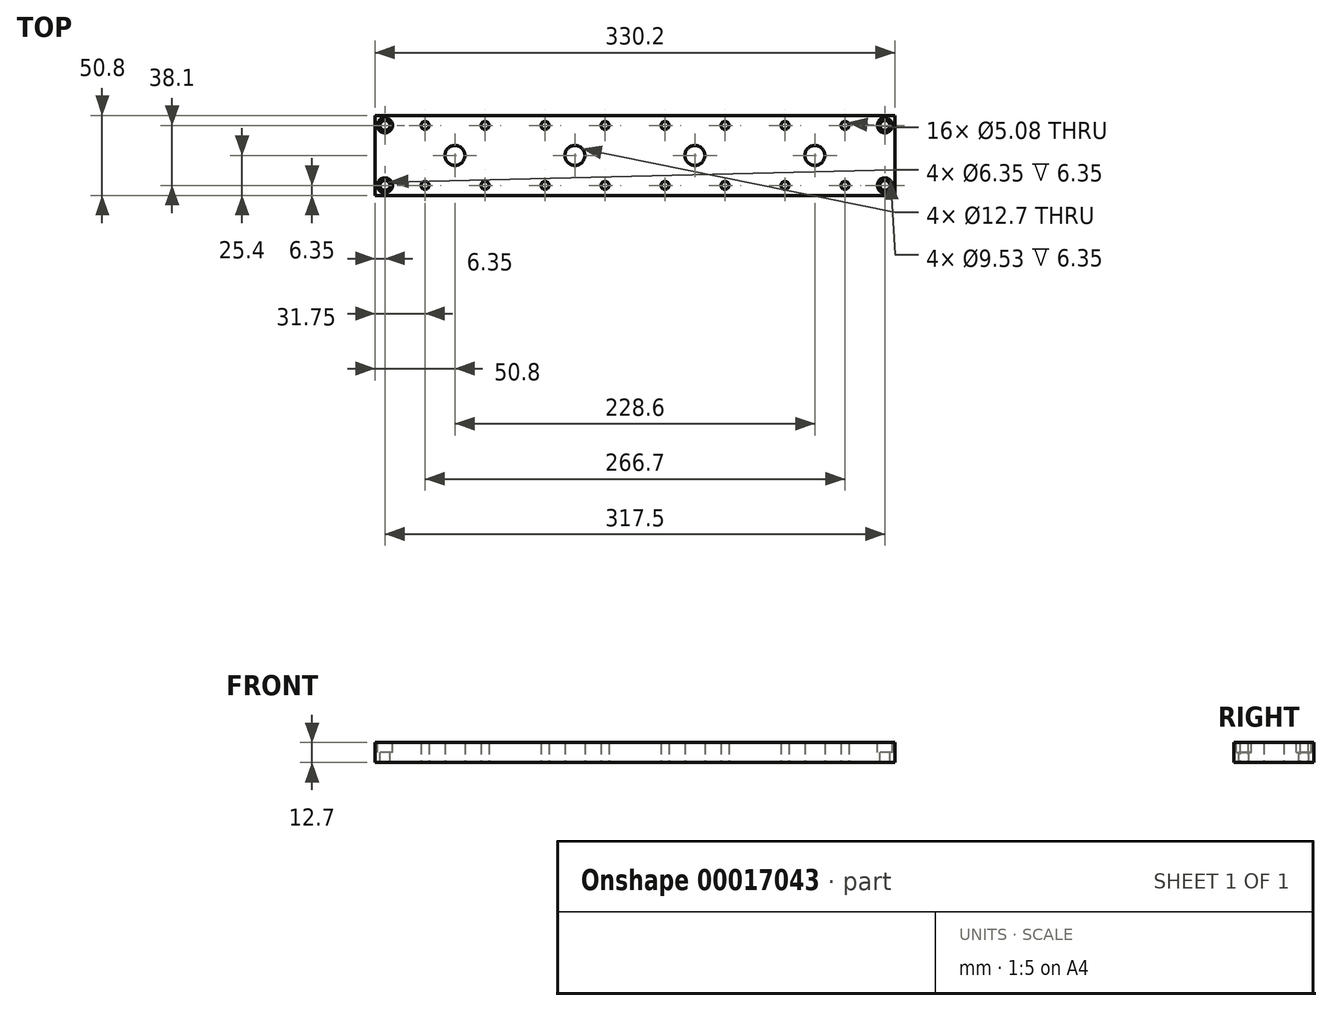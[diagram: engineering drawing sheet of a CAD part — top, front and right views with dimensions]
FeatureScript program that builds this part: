
annotation { "Feature Type Name" : "Feature", "Feature Type Description" : "" }
export const myFeature = defineFeature(function(context is Context, id is Id, definition is map)
    precondition{}
    {
        {
            var Q0;
            Q0=qCreatedBy(makeId("Top.planeOp"),FACE);
            var sketch = newSketch(context, id + "F0", { "sketchPlane" : qUnion([Q0])});
            skLineSegment(sketch, "E0.bottom", {"start": v(165.1, 25.4) * mm, "end": v(-165.1, 25.4) * mm});
            skLineSegment(sketch, "E0.top", {"start": v(165.1, -25.4) * mm, "end": v(-165.1, -25.4) * mm});
            skLineSegment(sketch, "E0.left", {"start": v(165.1, 25.4) * mm, "end": v(165.1, -25.4) * mm});
            skLineSegment(sketch, "E0.right", {"start": v(-165.1, 25.4) * mm, "end": v(-165.1, -25.4) * mm});
            skPoint(sketch, "E0.middle", {"position": v(0, 0) * mm});
            skCircle(sketch, "E1", {"center": v(-38.1, 0) * mm, "radius": 6.35 * mm});
            skCircle(sketch, "E2", {"center": v(-114.3, 0) * mm, "radius": 6.35 * mm});
            skCircle(sketch, "E3", {"center": v(38.1, 0) * mm, "radius": 6.35 * mm});
            skCircle(sketch, "E4", {"center": v(114.3, 0) * mm, "radius": 6.35 * mm});
            skCircle(sketch, "E5", {"center": v(-133.35, 19.05) * mm, "radius": 2.54 * mm});
            skCircle(sketch, "E6", {"center": v(-95.25, 19.05) * mm, "radius": 2.54 * mm});
            skCircle(sketch, "E7", {"center": v(-95.25, -19.05) * mm, "radius": 2.54 * mm});
            skCircle(sketch, "E8", {"center": v(-133.35, -19.05) * mm, "radius": 2.54 * mm});
            skCircle(sketch, "E9.1.0.0", {"center": v(-19.05, 19.05) * mm, "radius": 2.54 * mm});
            skCircle(sketch, "E9.1.0.1", {"center": v(-57.15, 19.05) * mm, "radius": 2.54 * mm});
            skCircle(sketch, "E9.1.0.2", {"center": v(-57.15, -19.05) * mm, "radius": 2.54 * mm});
            skCircle(sketch, "E9.1.0.3", {"center": v(-19.05, -19.05) * mm, "radius": 2.54 * mm});
            skCircle(sketch, "E9.2.0.0", {"center": v(57.15, 19.05) * mm, "radius": 2.54 * mm});
            skCircle(sketch, "E9.2.0.1", {"center": v(19.05, 19.05) * mm, "radius": 2.54 * mm});
            skCircle(sketch, "E9.2.0.2", {"center": v(19.05, -19.05) * mm, "radius": 2.54 * mm});
            skCircle(sketch, "E9.2.0.3", {"center": v(57.15, -19.05) * mm, "radius": 2.54 * mm});
            skCircle(sketch, "E9.3.0.0", {"center": v(133.35, 19.05) * mm, "radius": 2.54 * mm});
            skCircle(sketch, "E9.3.0.1", {"center": v(95.25, 19.05) * mm, "radius": 2.54 * mm});
            skCircle(sketch, "E9.3.0.2", {"center": v(95.25, -19.05) * mm, "radius": 2.54 * mm});
            skCircle(sketch, "E9.3.0.3", {"center": v(133.35, -19.05) * mm, "radius": 2.54 * mm});
            skLineSegment(sketch, "E9.direction1", {"start": v(-95.25, 19.05) * mm, "end": v(-19.05, 19.05) * mm, "construction": true});
            skSolve(sketch);
        }
        {
            var Q0;
            Q0 = qSketchRegion(id + "F0", true);
            extrude(context, id + "F1", {"entities" : qUnion([Q0]), "depth" : 12.7 * mm});
        }
        {
            var Q0;
            Q0=makeQuery(id+"F1.opExtrude","CAP_FACE",FACE,{"disambiguationData":[OSD([sQuery(id+"F0.wireOp",EDGE,"E0.bottom"),sQuery(id+"F0.wireOp",EDGE,"E0.top"),sQuery(id+"F0.wireOp",EDGE,"E0.left"),sQuery(id+"F0.wireOp",EDGE,"E0.right"),sQuery(id+"F0.wireOp",EDGE,"E1"),sQuery(id+"F0.wireOp",EDGE,"E2"),sQuery(id+"F0.wireOp",EDGE,"E3"),sQuery(id+"F0.wireOp",EDGE,"E4"),sQuery(id+"F0.wireOp",EDGE,"E5"),sQuery(id+"F0.wireOp",EDGE,"E6"),sQuery(id+"F0.wireOp",EDGE,"E7"),sQuery(id+"F0.wireOp",EDGE,"E8"),sQuery(id+"F0.wireOp",EDGE,"E9.1.0.0"),sQuery(id+"F0.wireOp",EDGE,"E9.1.0.1"),sQuery(id+"F0.wireOp",EDGE,"E9.1.0.2"),sQuery(id+"F0.wireOp",EDGE,"E9.1.0.3"),sQuery(id+"F0.wireOp",EDGE,"E9.2.0.0"),sQuery(id+"F0.wireOp",EDGE,"E9.2.0.1"),sQuery(id+"F0.wireOp",EDGE,"E9.2.0.2"),sQuery(id+"F0.wireOp",EDGE,"E9.2.0.3"),sQuery(id+"F0.wireOp",EDGE,"E9.3.0.0"),sQuery(id+"F0.wireOp",EDGE,"E9.3.0.1"),sQuery(id+"F0.wireOp",EDGE,"E9.3.0.2"),sQuery(id+"F0.wireOp",EDGE,"E9.3.0.3")])],"isStart":false});
            var sketch = newSketch(context, id + "F2", { "sketchPlane" : qUnion([Q0])});
            skCircle(sketch, "E10", {"center": v(-158.75, 19.05) * mm, "radius": 3.18 * mm});
            skCircle(sketch, "E11", {"center": v(-158.75, -19.05) * mm, "radius": 3.18 * mm});
            skCircle(sketch, "E12", {"center": v(158.75, -19.05) * mm, "radius": 3.18 * mm});
            skCircle(sketch, "E13", {"center": v(158.75, 19.05) * mm, "radius": 3.18 * mm});
            skSolve(sketch);
        }
        {
            var Q0;
            Q0 = qSketchRegion(id + "F2", true);
            extrude(context, id + "F3", {"entities" : qUnion([Q0]), "operationType" : NewBodyOperationType.REMOVE, "oppositeDirection" : true, "depth" : 25.4 * mm});
        }
        {
            var Q0;
            Q0=makeQuery(id+"F1.opExtrude","CAP_FACE",FACE,{"disambiguationData":[OSD([sQuery(id+"F0.wireOp",EDGE,"E0.bottom"),sQuery(id+"F0.wireOp",EDGE,"E0.top"),sQuery(id+"F0.wireOp",EDGE,"E0.left"),sQuery(id+"F0.wireOp",EDGE,"E0.right"),sQuery(id+"F0.wireOp",EDGE,"E1"),sQuery(id+"F0.wireOp",EDGE,"E2"),sQuery(id+"F0.wireOp",EDGE,"E3"),sQuery(id+"F0.wireOp",EDGE,"E4"),sQuery(id+"F0.wireOp",EDGE,"E5"),sQuery(id+"F0.wireOp",EDGE,"E6"),sQuery(id+"F0.wireOp",EDGE,"E7"),sQuery(id+"F0.wireOp",EDGE,"E8"),sQuery(id+"F0.wireOp",EDGE,"E9.1.0.0"),sQuery(id+"F0.wireOp",EDGE,"E9.1.0.1"),sQuery(id+"F0.wireOp",EDGE,"E9.1.0.2"),sQuery(id+"F0.wireOp",EDGE,"E9.1.0.3"),sQuery(id+"F0.wireOp",EDGE,"E9.2.0.0"),sQuery(id+"F0.wireOp",EDGE,"E9.2.0.1"),sQuery(id+"F0.wireOp",EDGE,"E9.2.0.2"),sQuery(id+"F0.wireOp",EDGE,"E9.2.0.3"),sQuery(id+"F0.wireOp",EDGE,"E9.3.0.0"),sQuery(id+"F0.wireOp",EDGE,"E9.3.0.1"),sQuery(id+"F0.wireOp",EDGE,"E9.3.0.2"),sQuery(id+"F0.wireOp",EDGE,"E9.3.0.3")])],"isStart":false});
            var sketch = newSketch(context, id + "F4", { "sketchPlane" : qUnion([Q0])});
            skCircle(sketch, "E14", {"center": v(-158.75, 19.05) * mm, "radius": 4.76 * mm});
            skCircle(sketch, "E15", {"center": v(-158.75, -19.05) * mm, "radius": 4.76 * mm});
            skCircle(sketch, "E16", {"center": v(158.75, -19.05) * mm, "radius": 4.76 * mm});
            skCircle(sketch, "E17", {"center": v(158.75, 19.05) * mm, "radius": 4.76 * mm});
            skSolve(sketch);
        }
        {
            var Q0;
            Q0 = qSketchRegion(id + "F4", true);
            extrude(context, id + "F5", {"entities" : qUnion([Q0]), "operationType" : NewBodyOperationType.REMOVE, "oppositeDirection" : true, "depth" : 6.35 * mm});
        }
    });
